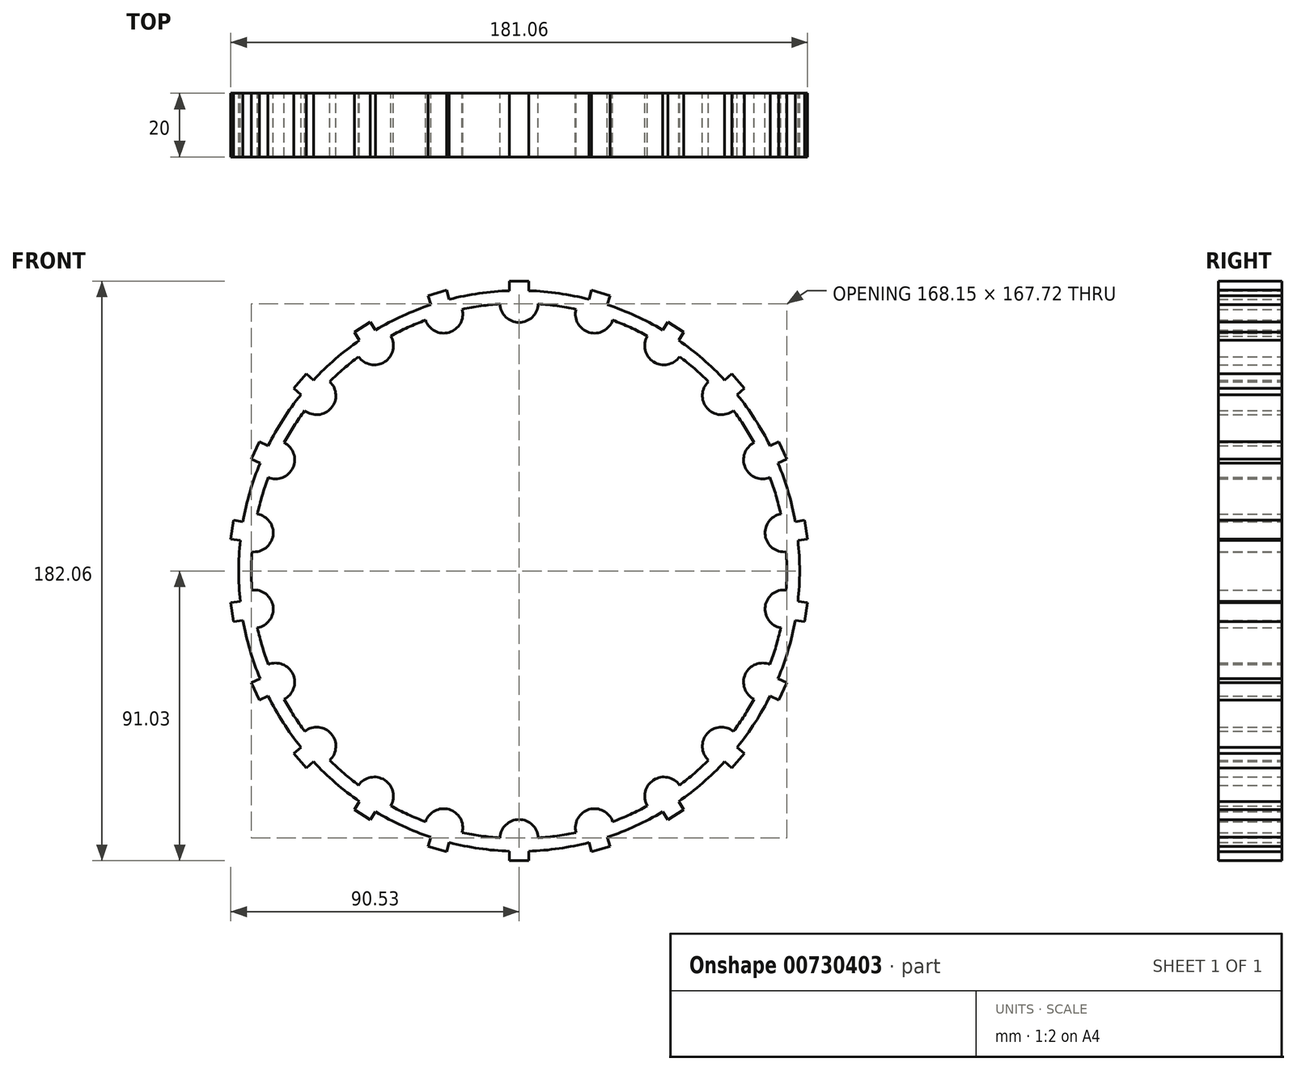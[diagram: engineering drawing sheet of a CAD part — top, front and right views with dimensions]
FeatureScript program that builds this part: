
annotation { "Feature Type Name" : "Feature", "Feature Type Description" : "" }
export const myFeature = defineFeature(function(context is Context, id is Id, definition is map)
    precondition{}
    {
        {
            var Q0;
            Q0=qCreatedBy(makeId("Front.planeOp"),FACE);
            var sketch = newSketch(context, id + "F0", { "sketchPlane" : qUnion([Q0])});
            skArc(sketch, "E0", {"start": v(11.97, 83.22) * mm, "mid": v(8.99, 83.6) * mm, "end": v(6, 83.86) * mm});
            skArc(sketch, "E1", {"start": v(-6, 83.86) * mm, "mid": v(0, 78.08) * mm, "end": v(6, 83.86) * mm});
            skPoint(sketch, "E2", {"position": v(-11.97, 83.22) * mm});
            skPoint(sketch, "E3", {"position": v(11.97, 83.22) * mm});
            skArc(sketch, "E4", {"start": v(-6, 83.86) * mm, "mid": v(-8.99, 83.6) * mm, "end": v(-11.97, 83.22) * mm});
            skArc(sketch, "E5", {"start": v(6, 83.86) * mm, "mid": v(0, 84.08) * mm, "end": v(-6, 83.86) * mm, "construction": true});
            skArc(sketch, "E6", {"start": v(12.53, 87.18) * mm, "mid": v(7.78, 87.73) * mm, "end": v(3, 88.03) * mm});
            skLineSegment(sketch, "E7", {"start": v(0, 0) * mm, "end": v(12.53, 87.18) * mm, "construction": true});
            skLineSegment(sketch, "E8", {"start": v(0, 0) * mm, "end": v(-12.53, 87.18) * mm, "construction": true});
            skLineSegment(sketch, "E9.top", {"start": v(-3, 91.03) * mm, "end": v(3, 91.03) * mm});
            skLineSegment(sketch, "E9.left", {"start": v(-3, 88.03) * mm, "end": v(-3, 91.03) * mm});
            skLineSegment(sketch, "E9.right", {"start": v(3, 88.03) * mm, "end": v(3, 91.03) * mm});
            skPoint(sketch, "E9.middle", {"position": v(0, 89.53) * mm});
            skArc(sketch, "E10.trimOffspring", {"start": v(-3, 88.03) * mm, "mid": v(-7.78, 87.73) * mm, "end": v(-12.53, 87.18) * mm});
            skArc(sketch, "E11.1.0", {"start": v(-27.68, 83.61) * mm, "mid": v(-32.18, 81.99) * mm, "end": v(-36.59, 80.12) * mm});
            skLineSegment(sketch, "E11.1.1", {"start": v(-27.68, 83.61) * mm, "end": v(-28.52, 86.5) * mm});
            skLineSegment(sketch, "E11.1.2", {"start": v(-28.52, 86.5) * mm, "end": v(-22.77, 88.18) * mm});
            skLineSegment(sketch, "E11.1.3", {"start": v(-21.92, 85.3) * mm, "end": v(-22.77, 88.18) * mm});
            skArc(sketch, "E11.1.4", {"start": v(-11.97, 83.22) * mm, "mid": v(-14.93, 82.74) * mm, "end": v(-17.87, 82.15) * mm});
            skArc(sketch, "E11.1.5", {"start": v(-29.38, 78.78) * mm, "mid": v(-22, 74.91) * mm, "end": v(-17.87, 82.15) * mm});
            skArc(sketch, "E11.1.6", {"start": v(-29.38, 78.78) * mm, "mid": v(-32.17, 77.68) * mm, "end": v(-34.93, 76.48) * mm});
            skArc(sketch, "E11.1.7", {"start": v(-12.53, 87.18) * mm, "mid": v(-17.25, 86.37) * mm, "end": v(-21.92, 85.3) * mm});
            skArc(sketch, "E11.2.0", {"start": v(-50.11, 72.43) * mm, "mid": v(-53.98, 69.6) * mm, "end": v(-57.68, 66.56) * mm});
            skLineSegment(sketch, "E11.2.1", {"start": v(-50.11, 72.43) * mm, "end": v(-51.74, 74.95) * mm});
            skLineSegment(sketch, "E11.2.2", {"start": v(-51.74, 74.95) * mm, "end": v(-46.69, 78.2) * mm});
            skLineSegment(sketch, "E11.2.3", {"start": v(-45.07, 75.67) * mm, "end": v(-46.69, 78.2) * mm});
            skArc(sketch, "E11.2.4", {"start": v(-34.93, 76.48) * mm, "mid": v(-37.63, 75.18) * mm, "end": v(-40.3, 73.8) * mm});
            skArc(sketch, "E11.2.5", {"start": v(-50.38, 67.3) * mm, "mid": v(-42.21, 65.68) * mm, "end": v(-40.3, 73.8) * mm});
            skArc(sketch, "E11.2.6", {"start": v(-50.38, 67.3) * mm, "mid": v(-52.75, 65.47) * mm, "end": v(-55.06, 63.54) * mm});
            skArc(sketch, "E11.2.7", {"start": v(-36.59, 80.12) * mm, "mid": v(-40.89, 78.01) * mm, "end": v(-45.07, 75.67) * mm});
            skArc(sketch, "E12.3.3.0", {"start": v(-68.49, 55.38) * mm, "mid": v(-71.4, 51.57) * mm, "end": v(-74.1, 47.62) * mm});
            skLineSegment(sketch, "E12.4.3.0", {"start": v(-68.49, 55.38) * mm, "end": v(-70.76, 57.34) * mm});
            skLineSegment(sketch, "E12.7.3.0", {"start": v(-70.76, 57.34) * mm, "end": v(-66.83, 61.88) * mm});
            skLineSegment(sketch, "E12.10.3.0", {"start": v(-64.56, 59.91) * mm, "end": v(-66.83, 61.88) * mm});
            skArc(sketch, "E12.13.3.0", {"start": v(-55.06, 63.54) * mm, "mid": v(-57.3, 61.53) * mm, "end": v(-59.45, 59.45) * mm});
            skArc(sketch, "E12.17.3.0", {"start": v(-67.3, 50.39) * mm, "mid": v(-59, 51.13) * mm, "end": v(-59.45, 59.45) * mm});
            skArc(sketch, "E12.21.3.0", {"start": v(-67.3, 50.39) * mm, "mid": v(-69.06, 47.95) * mm, "end": v(-70.73, 45.46) * mm});
            skArc(sketch, "E12.25.3.0", {"start": v(-57.68, 66.56) * mm, "mid": v(-61.2, 63.33) * mm, "end": v(-64.56, 59.91) * mm});
            skArc(sketch, "E13.3.4.0", {"start": v(-81.32, 33.84) * mm, "mid": v(-83.04, 29.37) * mm, "end": v(-84.5, 24.81) * mm});
            skLineSegment(sketch, "E13.4.4.0", {"start": v(-81.32, 33.84) * mm, "end": v(-84.05, 35.08) * mm});
            skLineSegment(sketch, "E13.7.4.0", {"start": v(-84.05, 35.08) * mm, "end": v(-81.55, 40.54) * mm});
            skLineSegment(sketch, "E13.10.4.0", {"start": v(-78.82, 39.3) * mm, "end": v(-81.55, 40.54) * mm});
            skArc(sketch, "E13.13.4.0", {"start": v(-70.73, 45.46) * mm, "mid": v(-72.3, 42.9) * mm, "end": v(-73.8, 40.3) * mm});
            skArc(sketch, "E13.17.4.0", {"start": v(-78.77, 29.38) * mm, "mid": v(-71.02, 32.43) * mm, "end": v(-73.8, 40.3) * mm});
            skArc(sketch, "E13.21.4.0", {"start": v(-78.77, 29.38) * mm, "mid": v(-79.77, 26.55) * mm, "end": v(-80.67, 23.69) * mm});
            skArc(sketch, "E13.25.4.0", {"start": v(-74.1, 47.62) * mm, "mid": v(-76.57, 43.52) * mm, "end": v(-78.82, 39.3) * mm});
            skArc(sketch, "E13.3.5.0", {"start": v(-87.56, 9.56) * mm, "mid": v(-87.95, 4.79) * mm, "end": v(-88.08, 0) * mm});
            skLineSegment(sketch, "E13.4.5.0", {"start": v(-87.56, 9.56) * mm, "end": v(-90.53, 9.98) * mm});
            skLineSegment(sketch, "E13.7.5.0", {"start": v(-90.53, 9.98) * mm, "end": v(-89.67, 15.92) * mm});
            skLineSegment(sketch, "E13.10.5.0", {"start": v(-86.7, 15.5) * mm, "end": v(-89.67, 15.92) * mm});
            skArc(sketch, "E13.13.5.0", {"start": v(-80.67, 23.69) * mm, "mid": v(-81.47, 20.8) * mm, "end": v(-82.16, 17.87) * mm});
            skArc(sketch, "E13.17.5.0", {"start": v(-83.86, 6) * mm, "mid": v(-77.28, 11.11) * mm, "end": v(-82.16, 17.87) * mm});
            skArc(sketch, "E13.21.5.0", {"start": v(-83.86, 6) * mm, "mid": v(-84.02, 3) * mm, "end": v(-84.08, 0) * mm});
            skArc(sketch, "E13.25.5.0", {"start": v(-84.5, 24.81) * mm, "mid": v(-85.73, 20.19) * mm, "end": v(-86.7, 15.5) * mm});
            skArc(sketch, "E13.3.6.0", {"start": v(-86.7, -15.5) * mm, "mid": v(-85.73, -20.19) * mm, "end": v(-84.5, -24.81) * mm});
            skLineSegment(sketch, "E13.4.6.0", {"start": v(-86.7, -15.5) * mm, "end": v(-89.67, -15.92) * mm});
            skLineSegment(sketch, "E13.7.6.0", {"start": v(-89.67, -15.92) * mm, "end": v(-90.53, -9.98) * mm});
            skLineSegment(sketch, "E13.10.6.0", {"start": v(-87.56, -9.56) * mm, "end": v(-90.53, -9.98) * mm});
            skArc(sketch, "E13.13.6.0", {"start": v(-84.08, 0) * mm, "mid": v(-84.02, -3) * mm, "end": v(-83.86, -6) * mm});
            skArc(sketch, "E13.17.6.0", {"start": v(-82.16, -17.87) * mm, "mid": v(-77.28, -11.11) * mm, "end": v(-83.86, -6) * mm});
            skArc(sketch, "E13.21.6.0", {"start": v(-82.16, -17.87) * mm, "mid": v(-81.47, -20.8) * mm, "end": v(-80.67, -23.69) * mm});
            skArc(sketch, "E13.25.6.0", {"start": v(-88.08, 0) * mm, "mid": v(-87.95, -4.79) * mm, "end": v(-87.56, -9.56) * mm});
            skArc(sketch, "E13.3.7.0", {"start": v(-78.82, -39.3) * mm, "mid": v(-76.57, -43.52) * mm, "end": v(-74.1, -47.62) * mm});
            skLineSegment(sketch, "E13.4.7.0", {"start": v(-78.82, -39.3) * mm, "end": v(-81.55, -40.54) * mm});
            skLineSegment(sketch, "E13.7.7.0", {"start": v(-81.55, -40.54) * mm, "end": v(-84.05, -35.08) * mm});
            skLineSegment(sketch, "E13.10.7.0", {"start": v(-81.32, -33.84) * mm, "end": v(-84.05, -35.08) * mm});
            skArc(sketch, "E13.13.7.0", {"start": v(-80.67, -23.69) * mm, "mid": v(-79.77, -26.55) * mm, "end": v(-78.77, -29.38) * mm});
            skArc(sketch, "E13.17.7.0", {"start": v(-73.8, -40.3) * mm, "mid": v(-71.02, -32.43) * mm, "end": v(-78.77, -29.38) * mm});
            skArc(sketch, "E13.21.7.0", {"start": v(-73.8, -40.3) * mm, "mid": v(-72.3, -42.9) * mm, "end": v(-70.73, -45.46) * mm});
            skArc(sketch, "E13.25.7.0", {"start": v(-84.5, -24.81) * mm, "mid": v(-83.04, -29.37) * mm, "end": v(-81.32, -33.84) * mm});
            skArc(sketch, "E13.3.8.0", {"start": v(-64.56, -59.91) * mm, "mid": v(-61.2, -63.33) * mm, "end": v(-57.68, -66.56) * mm});
            skLineSegment(sketch, "E13.4.8.0", {"start": v(-64.56, -59.91) * mm, "end": v(-66.83, -61.88) * mm});
            skLineSegment(sketch, "E13.7.8.0", {"start": v(-66.83, -61.88) * mm, "end": v(-70.76, -57.34) * mm});
            skLineSegment(sketch, "E13.10.8.0", {"start": v(-68.49, -55.38) * mm, "end": v(-70.76, -57.34) * mm});
            skArc(sketch, "E13.13.8.0", {"start": v(-70.73, -45.46) * mm, "mid": v(-69.06, -47.95) * mm, "end": v(-67.3, -50.39) * mm});
            skArc(sketch, "E13.17.8.0", {"start": v(-59.45, -59.45) * mm, "mid": v(-59, -51.13) * mm, "end": v(-67.3, -50.39) * mm});
            skArc(sketch, "E13.21.8.0", {"start": v(-59.45, -59.45) * mm, "mid": v(-57.3, -61.53) * mm, "end": v(-55.06, -63.54) * mm});
            skArc(sketch, "E13.25.8.0", {"start": v(-74.1, -47.62) * mm, "mid": v(-71.4, -51.57) * mm, "end": v(-68.49, -55.38) * mm});
            skArc(sketch, "E13.3.9.0", {"start": v(-45.07, -75.67) * mm, "mid": v(-40.89, -78.01) * mm, "end": v(-36.59, -80.12) * mm});
            skLineSegment(sketch, "E13.4.9.0", {"start": v(-45.07, -75.67) * mm, "end": v(-46.69, -78.2) * mm});
            skLineSegment(sketch, "E13.7.9.0", {"start": v(-46.69, -78.2) * mm, "end": v(-51.74, -74.95) * mm});
            skLineSegment(sketch, "E13.10.9.0", {"start": v(-50.11, -72.43) * mm, "end": v(-51.74, -74.95) * mm});
            skArc(sketch, "E13.13.9.0", {"start": v(-55.06, -63.54) * mm, "mid": v(-52.75, -65.47) * mm, "end": v(-50.38, -67.3) * mm});
            skArc(sketch, "E13.17.9.0", {"start": v(-40.3, -73.8) * mm, "mid": v(-42.21, -65.68) * mm, "end": v(-50.38, -67.3) * mm});
            skArc(sketch, "E13.21.9.0", {"start": v(-40.3, -73.8) * mm, "mid": v(-37.63, -75.18) * mm, "end": v(-34.93, -76.48) * mm});
            skArc(sketch, "E13.25.9.0", {"start": v(-57.68, -66.56) * mm, "mid": v(-53.98, -69.6) * mm, "end": v(-50.11, -72.43) * mm});
            skArc(sketch, "E13.3.10.0", {"start": v(-21.92, -85.3) * mm, "mid": v(-17.25, -86.37) * mm, "end": v(-12.53, -87.18) * mm});
            skLineSegment(sketch, "E13.4.10.0", {"start": v(-21.92, -85.3) * mm, "end": v(-22.77, -88.18) * mm});
            skLineSegment(sketch, "E13.7.10.0", {"start": v(-22.77, -88.18) * mm, "end": v(-28.52, -86.5) * mm});
            skLineSegment(sketch, "E13.10.10.0", {"start": v(-27.68, -83.61) * mm, "end": v(-28.52, -86.5) * mm});
            skArc(sketch, "E13.13.10.0", {"start": v(-34.93, -76.48) * mm, "mid": v(-32.17, -77.68) * mm, "end": v(-29.38, -78.78) * mm});
            skArc(sketch, "E13.17.10.0", {"start": v(-17.87, -82.15) * mm, "mid": v(-22, -74.91) * mm, "end": v(-29.38, -78.78) * mm});
            skArc(sketch, "E13.21.10.0", {"start": v(-17.87, -82.15) * mm, "mid": v(-14.93, -82.74) * mm, "end": v(-11.97, -83.22) * mm});
            skArc(sketch, "E13.25.10.0", {"start": v(-36.59, -80.12) * mm, "mid": v(-32.18, -81.99) * mm, "end": v(-27.68, -83.61) * mm});
            skArc(sketch, "E13.3.11.0", {"start": v(3, -88.03) * mm, "mid": v(7.78, -87.73) * mm, "end": v(12.53, -87.18) * mm});
            skLineSegment(sketch, "E13.4.11.0", {"start": v(3, -88.03) * mm, "end": v(3, -91.03) * mm});
            skLineSegment(sketch, "E13.7.11.0", {"start": v(3, -91.03) * mm, "end": v(-3, -91.03) * mm});
            skLineSegment(sketch, "E13.10.11.0", {"start": v(-3, -88.03) * mm, "end": v(-3, -91.03) * mm});
            skArc(sketch, "E13.13.11.0", {"start": v(-11.97, -83.22) * mm, "mid": v(-8.99, -83.6) * mm, "end": v(-6, -83.86) * mm});
            skArc(sketch, "E13.17.11.0", {"start": v(6, -83.86) * mm, "mid": v(0, -78.08) * mm, "end": v(-6, -83.86) * mm});
            skArc(sketch, "E13.21.11.0", {"start": v(6, -83.86) * mm, "mid": v(8.99, -83.6) * mm, "end": v(11.97, -83.22) * mm});
            skArc(sketch, "E13.25.11.0", {"start": v(-12.53, -87.18) * mm, "mid": v(-7.78, -87.73) * mm, "end": v(-3, -88.03) * mm});
            skArc(sketch, "E14.3.12.0", {"start": v(27.68, -83.61) * mm, "mid": v(32.18, -81.99) * mm, "end": v(36.59, -80.12) * mm});
            skLineSegment(sketch, "E14.4.12.0", {"start": v(27.68, -83.61) * mm, "end": v(28.52, -86.5) * mm});
            skLineSegment(sketch, "E14.7.12.0", {"start": v(28.52, -86.5) * mm, "end": v(22.77, -88.18) * mm});
            skLineSegment(sketch, "E14.10.12.0", {"start": v(21.92, -85.3) * mm, "end": v(22.77, -88.18) * mm});
            skArc(sketch, "E14.13.12.0", {"start": v(11.97, -83.22) * mm, "mid": v(14.93, -82.74) * mm, "end": v(17.87, -82.15) * mm});
            skArc(sketch, "E14.17.12.0", {"start": v(29.38, -78.78) * mm, "mid": v(22, -74.91) * mm, "end": v(17.87, -82.15) * mm});
            skArc(sketch, "E14.21.12.0", {"start": v(29.38, -78.78) * mm, "mid": v(32.17, -77.68) * mm, "end": v(34.93, -76.48) * mm});
            skArc(sketch, "E14.25.12.0", {"start": v(12.53, -87.18) * mm, "mid": v(17.25, -86.37) * mm, "end": v(21.92, -85.3) * mm});
            skArc(sketch, "E14.3.13.0", {"start": v(50.11, -72.43) * mm, "mid": v(53.98, -69.6) * mm, "end": v(57.68, -66.56) * mm});
            skLineSegment(sketch, "E14.4.13.0", {"start": v(50.11, -72.43) * mm, "end": v(51.74, -74.95) * mm});
            skLineSegment(sketch, "E14.7.13.0", {"start": v(51.74, -74.95) * mm, "end": v(46.69, -78.2) * mm});
            skLineSegment(sketch, "E14.10.13.0", {"start": v(45.07, -75.67) * mm, "end": v(46.69, -78.2) * mm});
            skArc(sketch, "E14.13.13.0", {"start": v(34.93, -76.48) * mm, "mid": v(37.63, -75.18) * mm, "end": v(40.3, -73.8) * mm});
            skArc(sketch, "E14.17.13.0", {"start": v(50.38, -67.3) * mm, "mid": v(42.21, -65.68) * mm, "end": v(40.3, -73.8) * mm});
            skArc(sketch, "E14.21.13.0", {"start": v(50.38, -67.3) * mm, "mid": v(52.75, -65.47) * mm, "end": v(55.06, -63.54) * mm});
            skArc(sketch, "E14.25.13.0", {"start": v(36.59, -80.12) * mm, "mid": v(40.89, -78.01) * mm, "end": v(45.07, -75.67) * mm});
            skArc(sketch, "E14.3.14.0", {"start": v(68.49, -55.38) * mm, "mid": v(71.4, -51.57) * mm, "end": v(74.1, -47.62) * mm});
            skLineSegment(sketch, "E14.4.14.0", {"start": v(68.49, -55.38) * mm, "end": v(70.76, -57.34) * mm});
            skLineSegment(sketch, "E14.7.14.0", {"start": v(70.76, -57.34) * mm, "end": v(66.83, -61.88) * mm});
            skLineSegment(sketch, "E14.10.14.0", {"start": v(64.56, -59.91) * mm, "end": v(66.83, -61.88) * mm});
            skArc(sketch, "E14.13.14.0", {"start": v(55.06, -63.54) * mm, "mid": v(57.3, -61.53) * mm, "end": v(59.45, -59.45) * mm});
            skArc(sketch, "E14.17.14.0", {"start": v(67.3, -50.39) * mm, "mid": v(59, -51.13) * mm, "end": v(59.45, -59.45) * mm});
            skArc(sketch, "E14.21.14.0", {"start": v(67.3, -50.39) * mm, "mid": v(69.06, -47.95) * mm, "end": v(70.73, -45.46) * mm});
            skArc(sketch, "E14.25.14.0", {"start": v(57.68, -66.56) * mm, "mid": v(61.2, -63.33) * mm, "end": v(64.56, -59.91) * mm});
            skArc(sketch, "E14.3.15.0", {"start": v(81.32, -33.84) * mm, "mid": v(83.04, -29.37) * mm, "end": v(84.5, -24.81) * mm});
            skLineSegment(sketch, "E14.4.15.0", {"start": v(81.32, -33.84) * mm, "end": v(84.05, -35.08) * mm});
            skLineSegment(sketch, "E14.7.15.0", {"start": v(84.05, -35.08) * mm, "end": v(81.55, -40.54) * mm});
            skLineSegment(sketch, "E14.10.15.0", {"start": v(78.82, -39.3) * mm, "end": v(81.55, -40.54) * mm});
            skArc(sketch, "E14.13.15.0", {"start": v(70.73, -45.46) * mm, "mid": v(72.3, -42.9) * mm, "end": v(73.8, -40.3) * mm});
            skArc(sketch, "E14.17.15.0", {"start": v(78.77, -29.38) * mm, "mid": v(71.02, -32.43) * mm, "end": v(73.8, -40.3) * mm});
            skArc(sketch, "E14.21.15.0", {"start": v(78.77, -29.38) * mm, "mid": v(79.77, -26.55) * mm, "end": v(80.67, -23.69) * mm});
            skArc(sketch, "E14.25.15.0", {"start": v(74.1, -47.62) * mm, "mid": v(76.57, -43.52) * mm, "end": v(78.82, -39.3) * mm});
            skArc(sketch, "E14.3.16.0", {"start": v(87.56, -9.56) * mm, "mid": v(87.95, -4.79) * mm, "end": v(88.08, 0) * mm});
            skLineSegment(sketch, "E14.4.16.0", {"start": v(87.56, -9.56) * mm, "end": v(90.53, -9.98) * mm});
            skLineSegment(sketch, "E14.7.16.0", {"start": v(90.53, -9.98) * mm, "end": v(89.67, -15.92) * mm});
            skLineSegment(sketch, "E14.10.16.0", {"start": v(86.7, -15.5) * mm, "end": v(89.67, -15.92) * mm});
            skArc(sketch, "E14.13.16.0", {"start": v(80.67, -23.69) * mm, "mid": v(81.47, -20.8) * mm, "end": v(82.16, -17.87) * mm});
            skArc(sketch, "E14.17.16.0", {"start": v(83.86, -6) * mm, "mid": v(77.28, -11.11) * mm, "end": v(82.16, -17.87) * mm});
            skArc(sketch, "E14.21.16.0", {"start": v(83.86, -6) * mm, "mid": v(84.02, -3) * mm, "end": v(84.08, 0) * mm});
            skArc(sketch, "E14.25.16.0", {"start": v(84.5, -24.81) * mm, "mid": v(85.73, -20.19) * mm, "end": v(86.7, -15.5) * mm});
            skArc(sketch, "E14.3.17.0", {"start": v(86.7, 15.5) * mm, "mid": v(85.73, 20.19) * mm, "end": v(84.5, 24.81) * mm});
            skLineSegment(sketch, "E14.4.17.0", {"start": v(86.7, 15.5) * mm, "end": v(89.67, 15.92) * mm});
            skLineSegment(sketch, "E14.7.17.0", {"start": v(89.67, 15.92) * mm, "end": v(90.53, 9.98) * mm});
            skLineSegment(sketch, "E14.10.17.0", {"start": v(87.56, 9.56) * mm, "end": v(90.53, 9.98) * mm});
            skArc(sketch, "E14.13.17.0", {"start": v(84.08, 0) * mm, "mid": v(84.02, 3) * mm, "end": v(83.86, 6) * mm});
            skArc(sketch, "E14.17.17.0", {"start": v(82.16, 17.87) * mm, "mid": v(77.28, 11.11) * mm, "end": v(83.86, 6) * mm});
            skArc(sketch, "E14.21.17.0", {"start": v(82.16, 17.87) * mm, "mid": v(81.47, 20.8) * mm, "end": v(80.67, 23.69) * mm});
            skArc(sketch, "E14.25.17.0", {"start": v(88.08, 0) * mm, "mid": v(87.95, 4.79) * mm, "end": v(87.56, 9.56) * mm});
            skArc(sketch, "E14.3.18.0", {"start": v(78.82, 39.3) * mm, "mid": v(76.57, 43.52) * mm, "end": v(74.1, 47.62) * mm});
            skLineSegment(sketch, "E14.4.18.0", {"start": v(78.82, 39.3) * mm, "end": v(81.55, 40.54) * mm});
            skLineSegment(sketch, "E14.7.18.0", {"start": v(81.55, 40.54) * mm, "end": v(84.05, 35.08) * mm});
            skLineSegment(sketch, "E14.10.18.0", {"start": v(81.32, 33.84) * mm, "end": v(84.05, 35.08) * mm});
            skArc(sketch, "E14.13.18.0", {"start": v(80.67, 23.69) * mm, "mid": v(79.77, 26.55) * mm, "end": v(78.77, 29.38) * mm});
            skArc(sketch, "E14.17.18.0", {"start": v(73.8, 40.3) * mm, "mid": v(71.02, 32.43) * mm, "end": v(78.77, 29.38) * mm});
            skArc(sketch, "E14.21.18.0", {"start": v(73.8, 40.3) * mm, "mid": v(72.3, 42.9) * mm, "end": v(70.73, 45.46) * mm});
            skArc(sketch, "E14.25.18.0", {"start": v(84.5, 24.81) * mm, "mid": v(83.04, 29.37) * mm, "end": v(81.32, 33.84) * mm});
            skArc(sketch, "E14.3.19.0", {"start": v(64.56, 59.91) * mm, "mid": v(61.2, 63.33) * mm, "end": v(57.68, 66.56) * mm});
            skLineSegment(sketch, "E14.4.19.0", {"start": v(64.56, 59.91) * mm, "end": v(66.83, 61.88) * mm});
            skLineSegment(sketch, "E14.7.19.0", {"start": v(66.83, 61.88) * mm, "end": v(70.76, 57.34) * mm});
            skLineSegment(sketch, "E14.10.19.0", {"start": v(68.49, 55.38) * mm, "end": v(70.76, 57.34) * mm});
            skArc(sketch, "E14.13.19.0", {"start": v(70.73, 45.46) * mm, "mid": v(69.06, 47.95) * mm, "end": v(67.3, 50.39) * mm});
            skArc(sketch, "E14.17.19.0", {"start": v(59.45, 59.45) * mm, "mid": v(59, 51.13) * mm, "end": v(67.3, 50.39) * mm});
            skArc(sketch, "E14.21.19.0", {"start": v(59.45, 59.45) * mm, "mid": v(57.3, 61.53) * mm, "end": v(55.06, 63.54) * mm});
            skArc(sketch, "E14.25.19.0", {"start": v(74.1, 47.62) * mm, "mid": v(71.4, 51.57) * mm, "end": v(68.49, 55.38) * mm});
            skArc(sketch, "E14.3.20.0", {"start": v(45.07, 75.67) * mm, "mid": v(40.89, 78.01) * mm, "end": v(36.59, 80.12) * mm});
            skLineSegment(sketch, "E14.4.20.0", {"start": v(45.07, 75.67) * mm, "end": v(46.69, 78.2) * mm});
            skLineSegment(sketch, "E14.7.20.0", {"start": v(46.69, 78.2) * mm, "end": v(51.74, 74.95) * mm});
            skLineSegment(sketch, "E14.10.20.0", {"start": v(50.11, 72.43) * mm, "end": v(51.74, 74.95) * mm});
            skArc(sketch, "E14.13.20.0", {"start": v(55.06, 63.54) * mm, "mid": v(52.75, 65.47) * mm, "end": v(50.38, 67.3) * mm});
            skArc(sketch, "E14.17.20.0", {"start": v(40.3, 73.8) * mm, "mid": v(42.21, 65.68) * mm, "end": v(50.38, 67.3) * mm});
            skArc(sketch, "E14.21.20.0", {"start": v(40.3, 73.8) * mm, "mid": v(37.63, 75.18) * mm, "end": v(34.93, 76.48) * mm});
            skArc(sketch, "E14.25.20.0", {"start": v(57.68, 66.56) * mm, "mid": v(53.98, 69.6) * mm, "end": v(50.11, 72.43) * mm});
            skArc(sketch, "E14.3.21.0", {"start": v(21.92, 85.3) * mm, "mid": v(17.25, 86.37) * mm, "end": v(12.53, 87.18) * mm});
            skLineSegment(sketch, "E14.4.21.0", {"start": v(21.92, 85.3) * mm, "end": v(22.77, 88.18) * mm});
            skLineSegment(sketch, "E14.7.21.0", {"start": v(22.77, 88.18) * mm, "end": v(28.52, 86.5) * mm});
            skLineSegment(sketch, "E14.10.21.0", {"start": v(27.68, 83.61) * mm, "end": v(28.52, 86.5) * mm});
            skArc(sketch, "E14.13.21.0", {"start": v(34.93, 76.48) * mm, "mid": v(32.17, 77.68) * mm, "end": v(29.38, 78.78) * mm});
            skArc(sketch, "E14.17.21.0", {"start": v(17.87, 82.15) * mm, "mid": v(22, 74.91) * mm, "end": v(29.38, 78.78) * mm});
            skArc(sketch, "E14.21.21.0", {"start": v(17.87, 82.15) * mm, "mid": v(14.93, 82.74) * mm, "end": v(11.97, 83.22) * mm});
            skArc(sketch, "E14.25.21.0", {"start": v(36.59, 80.12) * mm, "mid": v(32.18, 81.99) * mm, "end": v(27.68, 83.61) * mm});
            skSolve(sketch);
        }
        {
            var Q0;
            Q0 = qSketchRegion(id + "F0", true);
            extrude(context, id + "F1", {"entities" : qUnion([Q0]), "depth" : 20 * mm, "offsetDistance" : 25 * mm});
        }
    });
